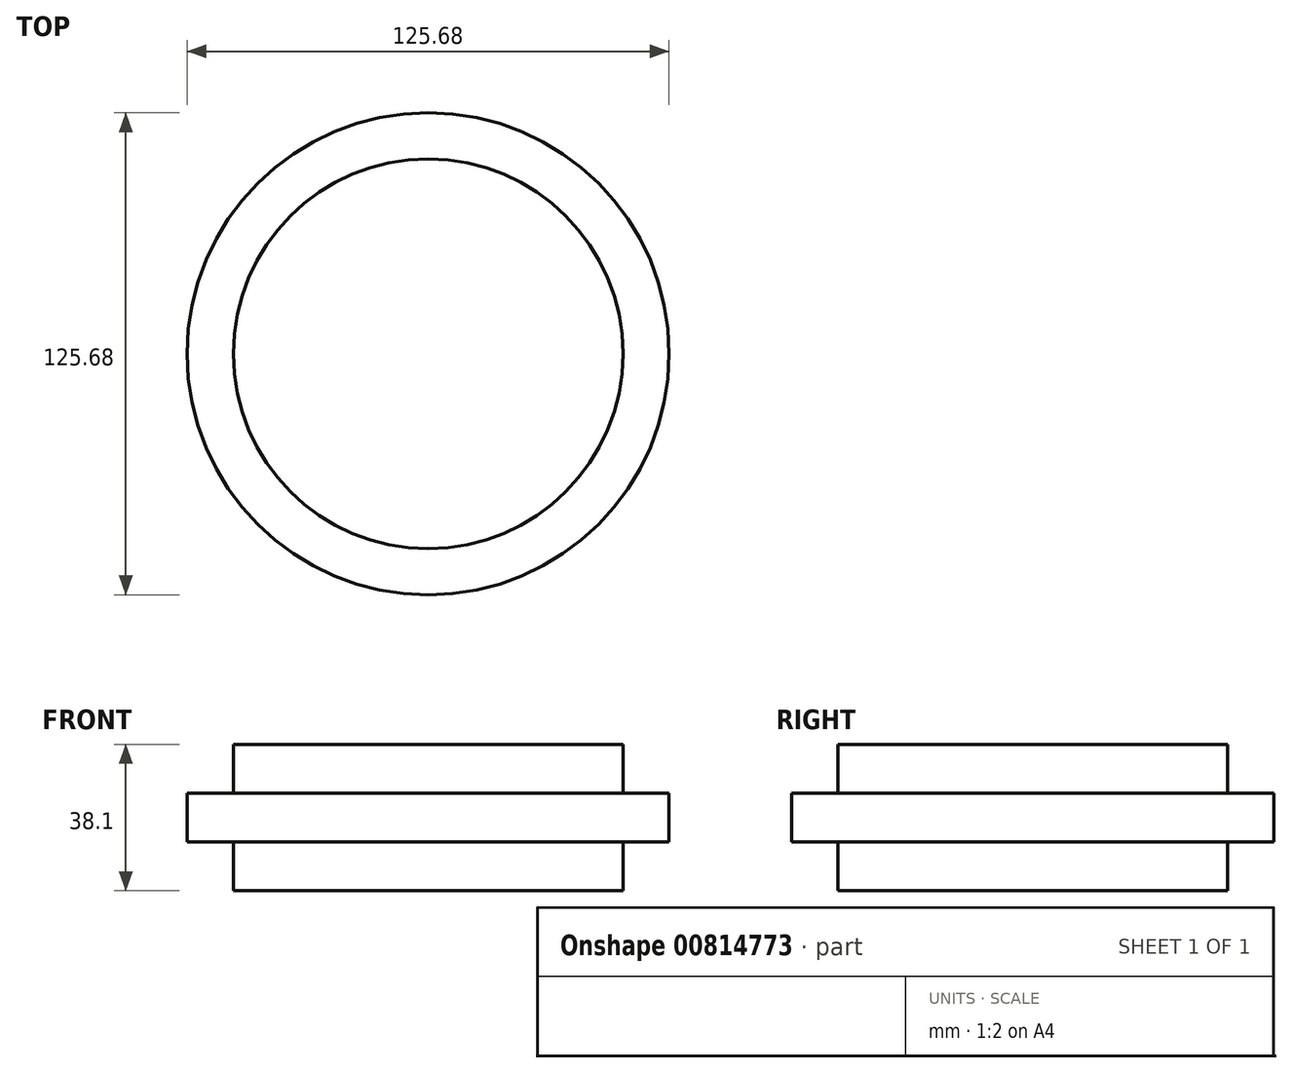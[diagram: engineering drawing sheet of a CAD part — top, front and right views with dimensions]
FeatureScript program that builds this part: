
annotation { "Feature Type Name" : "Feature", "Feature Type Description" : "" }
export const myFeature = defineFeature(function(context is Context, id is Id, definition is map)
    precondition{}
    {
        {
            var Q0;
            Q0=qCreatedBy(makeId("Front.planeOp"),FACE);
            var sketch = newSketch(context, id + "F0", { "sketchPlane" : qUnion([Q0])});
            skLineSegment(sketch, "E0", {"start": v(13.5, 25.4) * mm, "end": v(-37.3, 25.4) * mm});
            skLineSegment(sketch, "E1", {"start": v(-37.3, 25.4) * mm, "end": v(-37.3, 12.7) * mm});
            skLineSegment(sketch, "E2", {"start": v(-37.3, 12.7) * mm, "end": v(-49.33, 12.7) * mm});
            skLineSegment(sketch, "E3", {"start": v(-49.33, 12.7) * mm, "end": v(-49.33, 0) * mm});
            skLineSegment(sketch, "E4", {"start": v(-49.33, 0) * mm, "end": v(-37.3, 0) * mm});
            skLineSegment(sketch, "E5", {"start": v(-37.3, 0) * mm, "end": v(-37.3, -12.7) * mm});
            skLineSegment(sketch, "E6", {"start": v(-37.3, -12.7) * mm, "end": v(13.5, -12.7) * mm});
            skLineSegment(sketch, "E7", {"start": v(13.5, 25.4) * mm, "end": v(13.5, -12.7) * mm});
            skSolve(sketch);
        }
        {
            var Q0;
            Q0 = qSketchRegion(id + "F0", true);
            var Q1;
            Q1=sQuery(id+"F0.wireOp",EDGE,"E7");
            revolve(context, id + "F1", {"surfaceOperationType" : NewSurfaceOperationType.NEW, "entities" : qUnion([Q0]), "axis" : qUnion([Q1]), "revolveType" : RevolveType.FULL});
        }
    });
